# Revit family: TD92_FOR815_PRE009_RVT20_R00
name_source: partatom
category: Mobiliário
units: mm (PartAtom-declared; Revit-internal decimal feet)

## family parameters
Com base no plano de trabalho = Não
Compartilhado = Não
Corte com vazios quando carregada = Não
Número OmniClass = 23.40.20.00
Ponto de cálculo do ambiente = Não
Sempre na vertical = Sim
Título OmniClass = General Furniture and Specialties

## types (1)
- TD92_FOR815_PRE009_RVT20_R00
    Descrição = A Lixeira Tramontina T-Force 100L em Polipropileno garante praticidade para as atividades do dia a dia. Produzida em polipropileno, possui capacidade de 100 litros e características que a transformam na melhor escolha para suas necessidades. É uma lixeira articulável com superfície lisa, que facilita a limpeza. Possui tampa acionada por pedal e uma haste de acionamento resistente, que permite a mesma abertura de tampa por um longo período. Presente nos modelos com rodas e sem rodas.
    Elevação padrão = 0  [stored 0 ft]
    Fabricante = Tramontina Delta S/A
    Modelo = Lixeira Tramontina T-Force 100L com Rodas em Polipropileno Preto
    Nota-chave = 92815009
    URL = https://www.tramontinastore.com

note: [stored X ft] marks values corroborated as IEEE doubles in the binary element streams (Revit-internal decimal feet)
